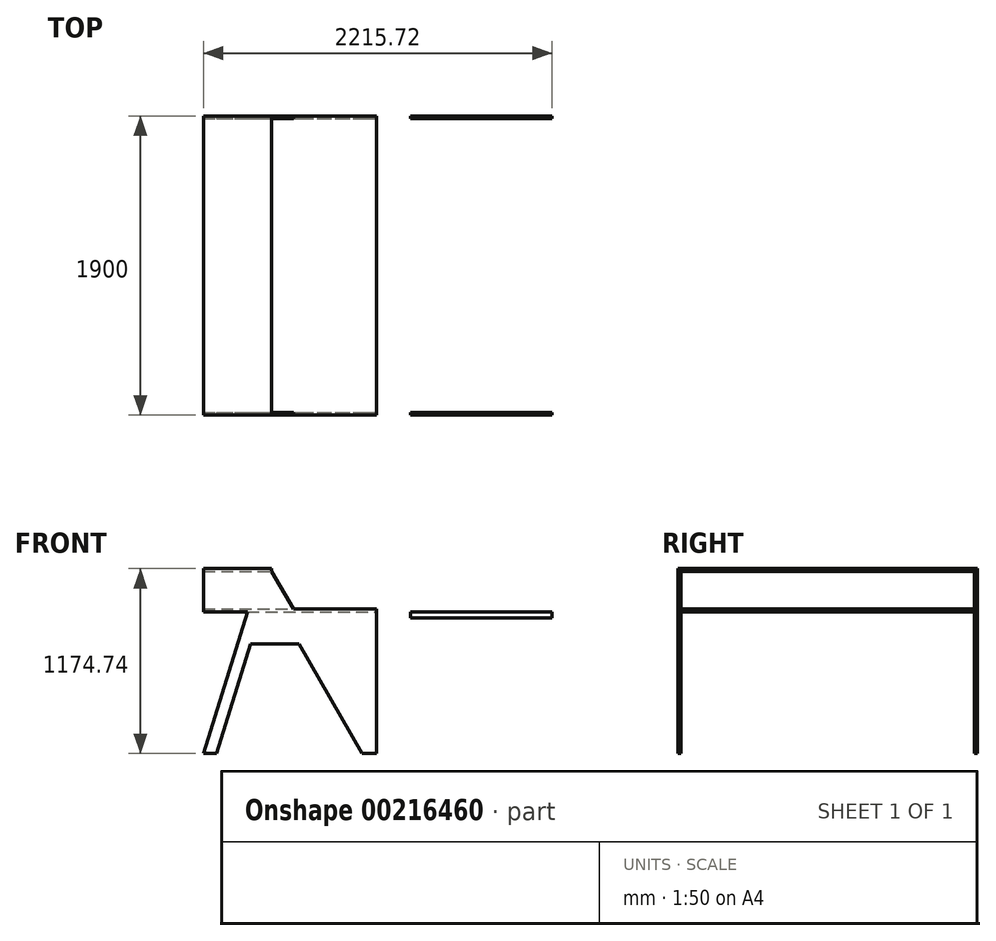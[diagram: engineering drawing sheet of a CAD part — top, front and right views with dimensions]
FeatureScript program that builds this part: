
annotation { "Feature Type Name" : "Feature", "Feature Type Description" : "" }
export const myFeature = defineFeature(function(context is Context, id is Id, definition is map)
    precondition{}
    {
        {
            var Q0;
            Q0=qCreatedBy(makeId("Top.planeOp"),FACE);
            var sketch = newSketch(context, id + "F0", { "sketchPlane" : qUnion([Q0])});
            skLineSegment(sketch, "E0.bottom", {"start": v(33.33, 0) * mm, "end": v(1133.33, 0) * mm});
            skLineSegment(sketch, "E0.top", {"start": v(33.33, 1900) * mm, "end": v(1133.33, 1900) * mm});
            skLineSegment(sketch, "E0.left", {"start": v(33.33, 0) * mm, "end": v(33.33, 1900) * mm});
            skLineSegment(sketch, "E0.right", {"start": v(1133.33, 0) * mm, "end": v(1133.33, 1900) * mm});
            skLineSegment(sketch, "E1.bottom", {"start": v(1349.05, 0) * mm, "end": v(2249.05, 0) * mm});
            skLineSegment(sketch, "E1.top", {"start": v(1349.05, 1900) * mm, "end": v(2249.05, 1900) * mm});
            skLineSegment(sketch, "E1.left", {"start": v(1349.05, 0) * mm, "end": v(1349.05, 1900) * mm});
            skLineSegment(sketch, "E1.right", {"start": v(2249.05, 0) * mm, "end": v(2249.05, 1900) * mm});
            skSolve(sketch);
        }
        {
            var Q0;
            Q0=makeQuery(id+"F0.imprint","IMPRINT",FACE,{"disambiguationData":[TD([[makeQuery(id+"F0.imprint","IMPRINT",EDGE,{"derivedFrom":sQuery(id+"F0.wireOp",EDGE,"E0.bottom")}),1.0]])]});
            extrude(context, id + "F1", {"entities" : qUnion([Q0]), "depth" : 1500 * mm});
        }
        {
            var Q0;
            Q0=makeQuery(id+"F0.imprint","IMPRINT",FACE,{"disambiguationData":[TD([[makeQuery(id+"F0.imprint","IMPRINT",EDGE,{"derivedFrom":sQuery(id+"F0.wireOp",EDGE,"E1.bottom")}),1.0]])]});
            extrude(context, id + "F2", {"entities" : qUnion([Q0]), "depth" : 900 * mm});
        }
        {
            var Q0;
            Q0=makeQuery(id+"F1.opExtrude","SWEPT_FACE",FACE,{"disambiguationData":[OSD([sQuery(id+"F0.wireOp",EDGE,"E0.bottom")])]});
            var sketch = newSketch(context, id + "F3", { "sketchPlane" : qUnion([Q0])});
            skLineSegment(sketch, "E2", {"start": v(33.33, 0) * mm, "end": v(313.4, 900) * mm});
            skLineSegment(sketch, "E3", {"start": v(117.12, 0) * mm, "end": v(397.19, 900) * mm});
            skLineSegment(sketch, "E4", {"start": v(397.19, 900) * mm, "end": v(769.47, 900) * mm});
            skLineSegment(sketch, "E5", {"start": v(583.33, -167.55) * mm, "end": v(583.33, -398.99) * mm, "construction": true});
            skPoint(sketch, "E5.startSnap0", {"position": v(583.33, 0) * mm});
            skLineSegment(sketch, "E6.bottom", {"start": v(33.33, 900) * mm, "end": v(1133.33, 900) * mm});
            skLineSegment(sketch, "E6.top", {"start": v(33.33, 918) * mm, "end": v(1133.33, 918) * mm});
            skLineSegment(sketch, "E6.left", {"start": v(33.33, 900) * mm, "end": v(33.33, 918) * mm});
            skLineSegment(sketch, "E6.right", {"start": v(1133.33, 900) * mm, "end": v(1133.33, 918) * mm});
            skLineSegment(sketch, "E7.bottom", {"start": v(33.33, 1174.74) * mm, "end": v(467.95, 1174.74) * mm});
            skLineSegment(sketch, "E7.top", {"start": v(33.33, 1155.74) * mm, "end": v(467.95, 1155.74) * mm});
            skLineSegment(sketch, "E7.left", {"start": v(33.33, 1174.74) * mm, "end": v(33.33, 1155.74) * mm});
            skLineSegment(sketch, "E7.right", {"start": v(467.95, 1174.74) * mm, "end": v(467.95, 1155.74) * mm});
            skLineSegment(sketch, "E8", {"start": v(467.95, 1155.74) * mm, "end": v(1133.33, 0) * mm});
            skLineSegment(sketch, "E9", {"start": v(375.64, 1155.74) * mm, "end": v(1041.02, 0) * mm});
            skLineSegment(sketch, "E10", {"start": v(33.33, 1174.74) * mm, "end": v(33.33, 900) * mm});
            skLineSegment(sketch, "E11", {"start": v(334.09, 697.23) * mm, "end": v(639.61, 697.23) * mm});
            skLineSegment(sketch, "E12", {"start": v(447.18, 1155.74) * mm, "end": v(584.05, 918) * mm});
            skLineSegment(sketch, "E13.bottom", {"start": v(1409.05, 0) * mm, "end": v(2189.05, 0) * mm});
            skLineSegment(sketch, "E13.top", {"start": v(1409.05, 860) * mm, "end": v(2189.05, 860) * mm});
            skLineSegment(sketch, "E13.left", {"start": v(1409.05, 0) * mm, "end": v(1409.05, 860) * mm});
            skLineSegment(sketch, "E13.right", {"start": v(2189.05, 0) * mm, "end": v(2189.05, 860) * mm});
            skPoint(sketch, "E14", {"position": v(1799.05, 0) * mm});
            skSolve(sketch);
        }
        {
            var Q0;
            {var subQ4=sQuery(id+"F3.wireOp",EDGE,"E7.bottom");Q0=makeQuery(id+"F3.imprint","IMPRINT",FACE,{"disambiguationData":[TD([[makeQuery(id+"F3.imprint","IMPRINT",EDGE,{"derivedFrom":subQ4}),1.0]])]});}
            var Q1;
            {var subQ3=sQuery(id+"F3.wireOp",EDGE,"E11");Q1=makeQuery(id+"F3.imprint","IMPRINT",FACE,{"disambiguationData":[TD([[makeQuery(id+"F3.imprint","IMPRINT",EDGE,{"derivedFrom":subQ3}),-1.0]])]});}
            var Q2;
            {var subQ0=sQuery(id+"F3.wireOp",EDGE,"E2");Q2=makeQuery(id+"F3.imprint","IMPRINT",FACE,{"disambiguationData":[TD([[makeQuery(id+"F3.imprint","IMPRINT",EDGE,{"derivedFrom":subQ0}),1.0]])]});}
            var Q3;
            {var subQ0=sQuery(id+"F3.wireOp",EDGE,"E6.bottom");var subQ1=makeQuery(id+"F3.imprint","IMPRINT",VERTEX,{"derivedFrom":subQ0});Q3=makeQuery(id+"F3.imprint","IMPRINT",FACE,{"disambiguationData":[TD([[makeQuery(id+"F3.imprint","IMPRINT",EDGE,{"disambiguationData":[TD([[subQ1,1.0]])],"derivedFrom":subQ0}),-1.0]])]});}
            var Q4;
            Q4=makeQuery(id+"F3.imprint","IMPRINT",FACE,{"disambiguationData":[TD([[makeQuery(id+"F3.imprint","IMPRINT",EDGE,{"derivedFrom":sQuery(id+"F3.wireOp",EDGE,"E13.bottom")}),1.0]])]});
            var Q5;
            Q5=sQuery(id+"F0.wireOp",VERTEX,"E0.left.end");
            extrude(context, id + "F4", {"entities" : qUnion([Q0, Q1, Q2, Q3, Q4]), "operationType" : NewBodyOperationType.REMOVE, "endBound" : BoundingType.UP_TO_VERTEX, "oppositeDirection" : true, "endBoundEntityVertex" : qUnion([Q5]), "depth" : 25 * mm});
        }
        {
            var Q0;
            {var subQ0=sQuery(id+"F3.wireOp",EDGE,"E10");var subQ1=sQuery(id+"F3.wireOp",EDGE,"E6.top");var subQ2=makeQuery(id+"F3.imprint","INTERSECT",VERTEX,{"derivedFrom":[subQ1,subQ0]});Q0=makeQuery(id+"F3.imprint","IMPRINT",FACE,{"disambiguationData":[TD([[makeQuery(id+"F3.imprint","IMPRINT",EDGE,{"disambiguationData":[TD([[subQ2,-1.0]])],"derivedFrom":subQ1}),1.0]])]});}
            var Q1;
            {var subQ0=sQuery(id+"F3.wireOp",EDGE,"E12");Q1=makeQuery(id+"F3.imprint","IMPRINT",FACE,{"disambiguationData":[TD([[makeQuery(id+"F3.imprint","IMPRINT",EDGE,{"derivedFrom":subQ0}),1.0]])]});}
            var Q2;
            {var subQ0=sQuery(id+"F3.wireOp",EDGE,"E12");Q2=makeQuery(id+"F3.imprint","IMPRINT",FACE,{"disambiguationData":[TD([[makeQuery(id+"F3.imprint","IMPRINT",EDGE,{"derivedFrom":subQ0}),-1.0]])]});}
            var Q3;
            {var subQ3=sQuery(id+"F3.wireOp",EDGE,"E11");Q3=makeQuery(id+"F3.imprint","IMPRINT",FACE,{"disambiguationData":[TD([[makeQuery(id+"F3.imprint","IMPRINT",EDGE,{"derivedFrom":subQ3}),1.0]])]});}
            extrude(context, id + "F5", {"entities" : qUnion([Q0, Q1, Q2, Q3]), "operationType" : NewBodyOperationType.REMOVE, "oppositeDirection" : true, "depth" : 1882 * mm, "hasSecondDirection" : true, "secondDirectionOppositeDirection" : true, "secondDirectionDepth" : 18 * mm});
        }
        {
            var Q0;
            Q0=makeQuery(id+"F2.opExtrude","SWEPT_FACE",FACE,{"disambiguationData":[OSD([sQuery(id+"F0.wireOp",EDGE,"E1.right")])]});
            var sketch = newSketch(context, id + "F6", { "sketchPlane" : qUnion([Q0])});
            skLineSegment(sketch, "E15.bottom", {"start": v(0, 0) * mm, "end": v(18, 0) * mm});
            skLineSegment(sketch, "E15.top", {"start": v(0, 900) * mm, "end": v(18, 900) * mm});
            skLineSegment(sketch, "E15.left", {"start": v(0, 0) * mm, "end": v(0, 900) * mm});
            skLineSegment(sketch, "E15.right", {"start": v(18, 0) * mm, "end": v(18, 900) * mm});
            skLineSegment(sketch, "E16.bottom", {"start": v(1900, 0) * mm, "end": v(1882, 0) * mm});
            skLineSegment(sketch, "E16.top", {"start": v(1900, 900) * mm, "end": v(1882, 900) * mm});
            skLineSegment(sketch, "E16.left", {"start": v(1900, 0) * mm, "end": v(1900, 900) * mm});
            skLineSegment(sketch, "E16.right", {"start": v(1882, 0) * mm, "end": v(1882, 900) * mm});
            skLineSegment(sketch, "E17.bottom", {"start": v(18, 900) * mm, "end": v(1882, 900) * mm});
            skLineSegment(sketch, "E17.top", {"start": v(18, 0) * mm, "end": v(1882, 0) * mm});
            skLineSegment(sketch, "E17.left", {"start": v(18, 900) * mm, "end": v(18, 0) * mm});
            skLineSegment(sketch, "E17.right", {"start": v(1882, 900) * mm, "end": v(1882, 0) * mm});
            skSolve(sketch);
        }
        {
            var Q0;
            Q0=makeQuery(id+"F6.imprint","IMPRINT",FACE,{"disambiguationData":[TD([[makeQuery(id+"F6.imprint","IMPRINT",EDGE,{"derivedFrom":sQuery(id+"F6.wireOp",EDGE,"E17.bottom")}),-1.0]])]});
            extrude(context, id + "F7", {"entities" : qUnion([Q0]), "operationType" : NewBodyOperationType.REMOVE, "oppositeDirection" : true, "depth" : 2750 * mm});
        }
        {
            var Q0;
            Q0=makeQuery(id+"F2.opExtrude","SWEPT_FACE",FACE,{"disambiguationData":[OSD([sQuery(id+"F0.wireOp",EDGE,"E1.right")])]});
            var sketch = newSketch(context, id + "F8", { "sketchPlane" : qUnion([Q0])});
            skLineSegment(sketch, "E18.bottom", {"start": v(216.56, 0) * mm, "end": v(276.56, 0) * mm});
            skLineSegment(sketch, "E18.top", {"start": v(216.56, 900) * mm, "end": v(276.56, 900) * mm});
            skLineSegment(sketch, "E18.left", {"start": v(216.56, 0) * mm, "end": v(216.56, 900) * mm});
            skLineSegment(sketch, "E18.right", {"start": v(276.56, 0) * mm, "end": v(276.56, 900) * mm});
            skLineSegment(sketch, "E19", {"start": v(950, -129.23) * mm, "end": v(950, -415.35) * mm, "construction": true});
            skPoint(sketch, "E19.startSnap0", {"position": v(950, 0) * mm});
            skLineSegment(sketch, "E20.MirrorCS", {"start": v(1683.44, 0) * mm, "end": v(1683.44, 900) * mm});
            skLineSegment(sketch, "E21.MirrorCS", {"start": v(1683.44, 0) * mm, "end": v(1623.44, 0) * mm});
            skLineSegment(sketch, "E22.MirrorCS", {"start": v(1623.44, 0) * mm, "end": v(1623.44, 900) * mm});
            skLineSegment(sketch, "E23.MirrorCS", {"start": v(1683.44, 900) * mm, "end": v(1623.44, 900) * mm});
            skLineSegment(sketch, "E24.bottom", {"start": v(216.56, 0) * mm, "end": v(0, 0) * mm});
            skLineSegment(sketch, "E24.top", {"start": v(216.56, 900) * mm, "end": v(0, 900) * mm});
            skLineSegment(sketch, "E24.right", {"start": v(0, 0) * mm, "end": v(0, 900) * mm});
            skLineSegment(sketch, "E25.bottom", {"start": v(276.56, 0) * mm, "end": v(1623.44, 0) * mm});
            skLineSegment(sketch, "E25.top", {"start": v(276.56, 900) * mm, "end": v(1623.44, 900) * mm});
            skLineSegment(sketch, "E26.bottom", {"start": v(1683.44, 0) * mm, "end": v(1900, 0) * mm});
            skLineSegment(sketch, "E26.top", {"start": v(1683.44, 900) * mm, "end": v(1900, 900) * mm});
            skLineSegment(sketch, "E26.right", {"start": v(1900, 0) * mm, "end": v(1900, 900) * mm});
            skLineSegment(sketch, "E27.bottom", {"start": v(0, 900) * mm, "end": v(1900, 900) * mm});
            skLineSegment(sketch, "E27.top", {"start": v(0, 860) * mm, "end": v(1900, 860) * mm});
            skLineSegment(sketch, "E27.left", {"start": v(0, 900) * mm, "end": v(0, 860) * mm});
            skLineSegment(sketch, "E27.right", {"start": v(1900, 900) * mm, "end": v(1900, 860) * mm});
            skSolve(sketch);
        }
        {
            var Q0;
            {var subQ0=sQuery(id+"F8.wireOp",EDGE,"E24.bottom");Q0=makeQuery(id+"F8.imprint","IMPRINT",FACE,{"disambiguationData":[TD([[makeQuery(id+"F8.imprint","IMPRINT",EDGE,{"derivedFrom":subQ0}),1.0]])]});}
            var Q1;
            {var subQ0=sQuery(id+"F8.wireOp",EDGE,"E25.bottom");Q1=makeQuery(id+"F8.imprint","IMPRINT",FACE,{"disambiguationData":[TD([[makeQuery(id+"F8.imprint","IMPRINT",EDGE,{"derivedFrom":subQ0}),1.0]])]});}
            var Q2;
            {var subQ0=sQuery(id+"F8.wireOp",EDGE,"E26.bottom");Q2=makeQuery(id+"F8.imprint","IMPRINT",FACE,{"disambiguationData":[TD([[makeQuery(id+"F8.imprint","IMPRINT",EDGE,{"derivedFrom":subQ0}),1.0]])]});}
            var Q3;
            Q3=sQuery(id+"F0.wireOp",VERTEX,"E1.left.start");
            extrude(context, id + "F9", {"entities" : qUnion([Q0, Q1, Q2]), "operationType" : NewBodyOperationType.REMOVE, "endBound" : BoundingType.UP_TO_VERTEX, "oppositeDirection" : true, "endBoundEntityVertex" : qUnion([Q3]), "depth" : 493 * mm});
        }
    });
